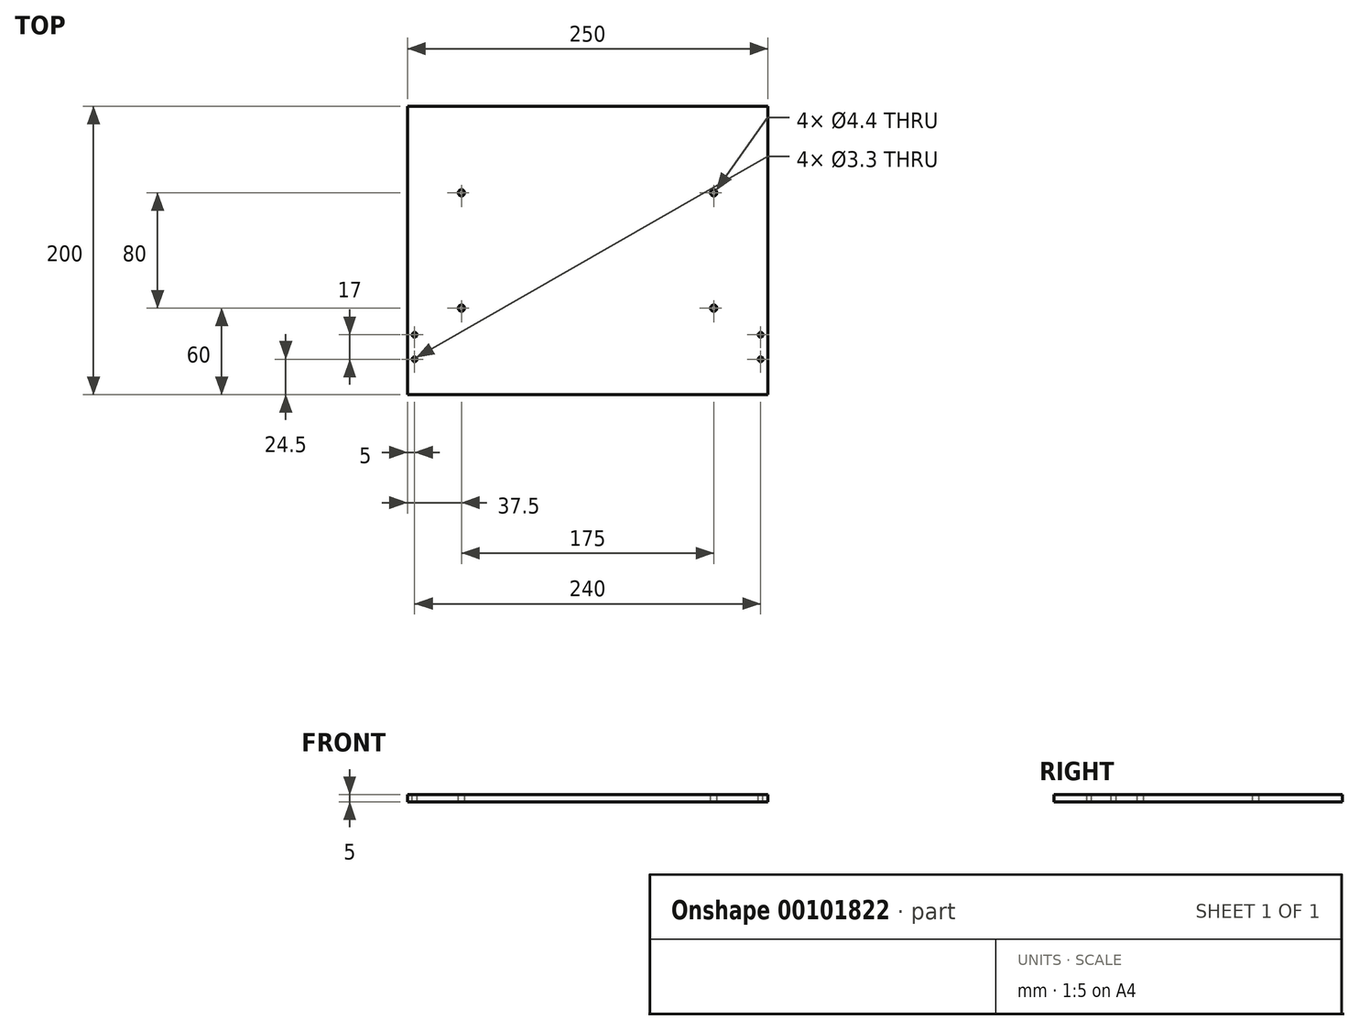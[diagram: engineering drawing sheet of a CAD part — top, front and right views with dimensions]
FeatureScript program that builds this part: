
annotation { "Feature Type Name" : "Feature", "Feature Type Description" : "" }
export const myFeature = defineFeature(function(context is Context, id is Id, definition is map)
    precondition{}
    {
        {
            var Q0;
            Q0=qCreatedBy(makeId("Top.planeOp"),FACE);
            var sketch = newSketch(context, id + "F0", { "sketchPlane" : qUnion([Q0])});
            skLineSegment(sketch, "E0.bottom", {"start": v(-125, 100) * mm, "end": v(125, 100) * mm});
            skLineSegment(sketch, "E0.top", {"start": v(-125, -100) * mm, "end": v(125, -100) * mm});
            skLineSegment(sketch, "E0.left", {"start": v(-125, 100) * mm, "end": v(-125, -100) * mm});
            skLineSegment(sketch, "E0.right", {"start": v(125, 100) * mm, "end": v(125, -100) * mm});
            skPoint(sketch, "E0.middle", {"position": v(0, 0) * mm});
            skLineSegment(sketch, "E1.bottom", {"start": v(-75, 75) * mm, "end": v(75, 75) * mm, "construction": true});
            skLineSegment(sketch, "E1.top", {"start": v(-75, -75) * mm, "end": v(75, -75) * mm, "construction": true});
            skLineSegment(sketch, "E1.left", {"start": v(-75, 75) * mm, "end": v(-75, -75) * mm, "construction": true});
            skLineSegment(sketch, "E1.right", {"start": v(75, 75) * mm, "end": v(75, -75) * mm, "construction": true});
            skPoint(sketch, "E2", {"position": v(-87.5, 40) * mm});
            skLineSegment(sketch, "E3", {"start": v(125, 0) * mm, "end": v(-125, 0) * mm, "construction": true});
            skLineSegment(sketch, "E4", {"start": v(0, 100) * mm, "end": v(0, -100) * mm, "construction": true});
            skPoint(sketch, "E5.MirrorP", {"position": v(87.5, 40) * mm});
            skPoint(sketch, "E6.MirrorP", {"position": v(-87.5, -40) * mm});
            skPoint(sketch, "E7.MirrorP", {"position": v(87.5, -40) * mm});
            skLineSegment(sketch, "E8", {"start": v(-125, -67) * mm, "end": v(125, -67) * mm, "construction": true});
            skLineSegment(sketch, "E9.bottom", {"start": v(-115, -54) * mm, "end": v(-125, -54) * mm, "construction": true});
            skLineSegment(sketch, "E9.top", {"start": v(-115, -80) * mm, "end": v(-125, -80) * mm, "construction": true});
            skLineSegment(sketch, "E9.left", {"start": v(-115, -54) * mm, "end": v(-115, -80) * mm, "construction": true});
            skLineSegment(sketch, "E9.right", {"start": v(-125, -54) * mm, "end": v(-125, -80) * mm});
            skPoint(sketch, "E9.middle", {"position": v(-120, -67) * mm});
            skLineSegment(sketch, "E10", {"start": v(-120, -54) * mm, "end": v(-120, -80) * mm, "construction": true});
            skPoint(sketch, "E11", {"position": v(-120, -58.5) * mm});
            skPoint(sketch, "E12.MirrorP", {"position": v(-120, -75.5) * mm});
            skPoint(sketch, "E13.MirrorP", {"position": v(120, -58.5) * mm});
            skPoint(sketch, "E14.MirrorP", {"position": v(120, -75.5) * mm});
            skSolve(sketch);
        }
        {
            var Q0;
            Q0=makeQuery(id+"F0.imprint","IMPRINT",FACE,{"disambiguationData":[TD([[makeQuery(id+"F0.imprint","IMPRINT",EDGE,{"derivedFrom":sQuery(id+"F0.wireOp",EDGE,"E0.bottom")}),-1.0]])]});
            extrude(context, id + "F1", {"entities" : qUnion([Q0]), "depth" : 5 * mm});
        }
        {
            var Q0;
            Q0=sQuery(id+"F0.wireOp",VERTEX,"E2");
            var Q1;
            Q1=sQuery(id+"F0.wireOp",VERTEX,"E5.MirrorP");
            var Q2;
            Q2=sQuery(id+"F0.wireOp",VERTEX,"E6.MirrorP");
            var Q3;
            Q3=sQuery(id+"F0.wireOp",VERTEX,"E7.MirrorP");
            var Q4;
            Q4=makeQuery(id+"F1.opExtrude","SWEPT_BODY",BODY,{"disambiguationData":[OSD([sQuery(id+"F0.wireOp",EDGE,"E0.bottom"),sQuery(id+"F0.wireOp",EDGE,"E0.top"),sQuery(id+"F0.wireOp",EDGE,"E0.left"),sQuery(id+"F0.wireOp",EDGE,"E0.right")])]});
            hole(context, id + "F2", {"style" : HoleStyle.SIMPLE, "endStyle" : HoleEndStyle.THROUGH, "oppositeDirection" : true, "standardTappedOrClearance" : lookupTablePath({ "standard" : "ISO", "fit" : "Normal", "size" : "M4", "type" : "Clearance" }), "standardBlindInLast" : lookupTablePath({ "fit" : "Standard", "standard" : "ISO", "size" : "M4", "type" : "Clearance" }), "holeDiameter" : 4.4 * mm, "locations" : qUnion([Q0, Q1, Q2, Q3]), "scope" : qUnion([Q4]), "isTappedThrough" : true});
        }
        {
            var Q0;
            Q0=sQuery(id+"F0.wireOp",VERTEX,"E11");
            var Q1;
            Q1=sQuery(id+"F0.wireOp",VERTEX,"E12.MirrorP");
            var Q2;
            Q2=sQuery(id+"F0.wireOp",VERTEX,"E14.MirrorP");
            var Q3;
            Q3=sQuery(id+"F0.wireOp",VERTEX,"E13.MirrorP");
            var Q4;
            Q4=makeQuery(id+"F1.opExtrude","SWEPT_BODY",BODY,{"disambiguationData":[OSD([sQuery(id+"F0.wireOp",EDGE,"E0.bottom"),sQuery(id+"F0.wireOp",EDGE,"E0.top"),sQuery(id+"F0.wireOp",EDGE,"E0.left"),sQuery(id+"F0.wireOp",EDGE,"E0.right"),sQuery(id+"F0.wireOp",EDGE,"E9.bottom"),sQuery(id+"F0.wireOp",EDGE,"E9.top"),sQuery(id+"F0.wireOp",EDGE,"E9.left")])]});
            hole(context, id + "F3", {"style" : HoleStyle.SIMPLE, "endStyle" : HoleEndStyle.THROUGH, "oppositeDirection" : true, "standardTappedOrClearance" : lookupTablePath({ "standard" : "ISO", "fit" : "Normal", "size" : "M3", "type" : "Clearance" }), "standardBlindInLast" : lookupTablePath({ "fit" : "Standard", "standard" : "ISO", "size" : "M3", "type" : "Clearance" }), "holeDiameter" : 3.3 * mm, "locations" : qUnion([Q0, Q1, Q2, Q3]), "scope" : qUnion([Q4]), "isTappedThrough" : true});
        }
    });
